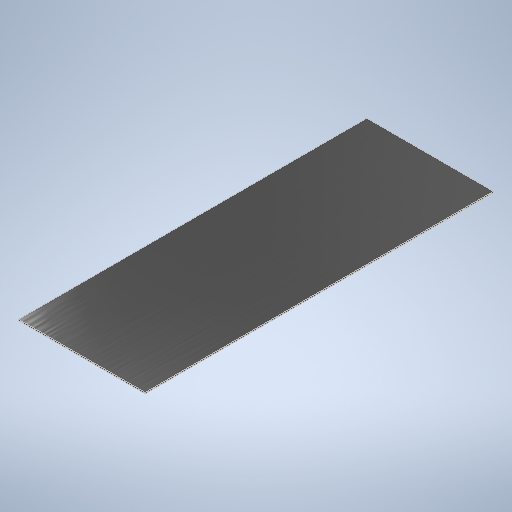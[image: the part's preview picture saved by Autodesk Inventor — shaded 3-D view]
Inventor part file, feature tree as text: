
AUTODESK INVENTOR PART (.ipt)
format: ipt  version: 2025.1 (Build 291241020, 241B)  size: 239,104 bytes
history: native  units: in
note: dims shown in document units (in); Inventor stores cm internally (conversion verified against a paired STEP export)
features: extrude x1, sketch x1
ambient origin geometry x8: Origin, YZ Plane, XZ Plane, XY Plane, X Axis, Y Axis, Z Axis, Center Point
bodies: Solid1 (feature_tree)
feature tree (2):
  extrude  "Extrusion1"  Depth=36.45in
  sketch  "Sketch1"  dims[d0=13.25in d1=36.45in d2=0.125in d3=0.0in]
